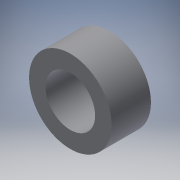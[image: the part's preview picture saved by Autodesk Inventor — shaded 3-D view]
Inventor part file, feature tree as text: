
AUTODESK INVENTOR PART (.ipt)
format: ipt  version: 2016 (Build 200138000, 138)  size: 97,280 bytes
history: native  units: in
note: dims shown in document units (in); Inventor stores cm internally (conversion verified against a paired STEP export)
features: extrude x1, sketch x1
ambient origin geometry x8: Origin, YZ Plane, XZ Plane, XY Plane, X Axis, Y Axis, Z Axis, Center Point
bodies: Solid1 (feature_tree)
feature tree (2):
  extrude  "Extrusion1"  Depth=0.235in
  sketch  "Sketch1"  dims[d0=0.375in d1=0.125in d2=0.235in d3=0.0in]
